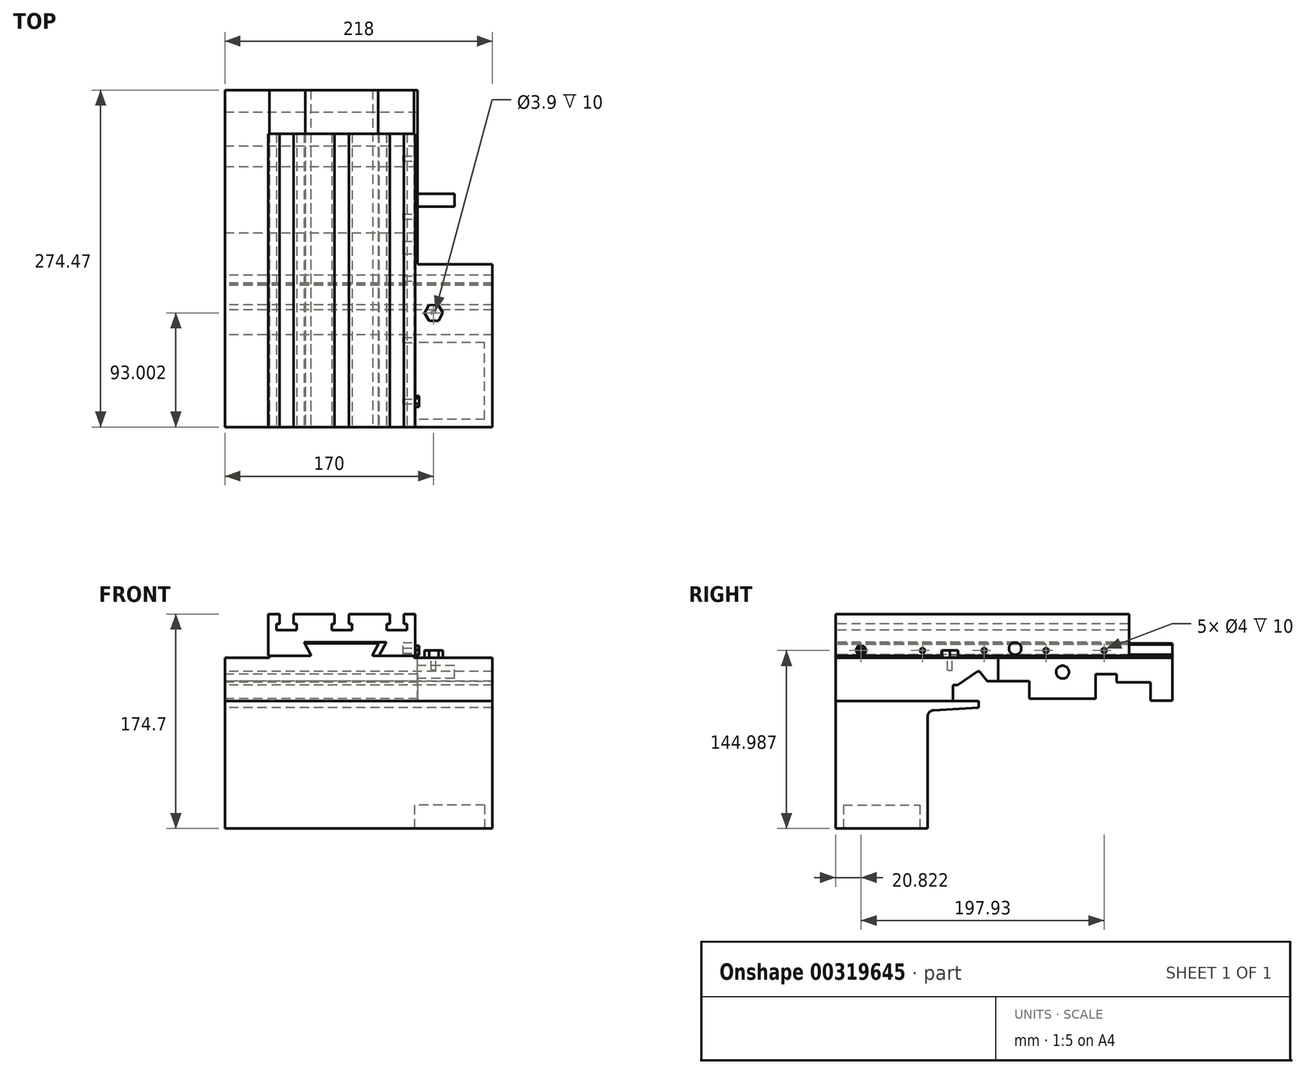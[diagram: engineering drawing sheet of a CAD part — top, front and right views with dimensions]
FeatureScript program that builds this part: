
annotation { "Feature Type Name" : "Feature", "Feature Type Description" : "" }
export const myFeature = defineFeature(function(context is Context, id is Id, definition is map)
    precondition{}
    {
        {
            var Q0;
            Q0=qCreatedBy(makeId("Right.planeOp"),FACE);
            var sketch = newSketch(context, id + "F0", { "sketchPlane" : qUnion([Q0])});
            skLineSegment(sketch, "E0", {"start": v(34.05, 18.4) * mm, "end": v(34.05, 3.4) * mm});
            skLineSegment(sketch, "E1", {"start": v(-63.5, 18.4) * mm, "end": v(-63.5, 3.9) * mm});
            skLineSegment(sketch, "E2", {"start": v(37.05, 18.4) * mm, "end": v(11.3, 18.4) * mm});
            skLineSegment(sketch, "E3", {"start": v(-63.5, 18.4) * mm, "end": v(-90.75, 18.4) * mm});
            skLineSegment(sketch, "E4", {"start": v(-96.5, 16.9) * mm, "end": v(-96.5, 20.4) * mm});
            skLineSegment(sketch, "E5", {"start": v(-96.5, 16.9) * mm, "end": v(-92.5, 16.9) * mm});
            skLineSegment(sketch, "E6", {"start": v(-63.5, 3.9) * mm, "end": v(-72.5, 3.9) * mm});
            skLineSegment(sketch, "E7", {"start": v(-72.5, 3.9) * mm, "end": v(-72.5, -0.6) * mm});
            skLineSegment(sketch, "E8", {"start": v(-90.75, 18.4) * mm, "end": v(-92.5, 16.9) * mm});
            skLineSegment(sketch, "E9", {"start": v(-95.7, 19.4) * mm, "end": v(-102.04, 27.24) * mm});
            skLineSegment(sketch, "E10", {"start": v(-100.9, 25.84) * mm, "end": v(-105.9, 25.84) * mm});
            skLineSegment(sketch, "E11", {"start": v(-103.87, 27.24) * mm, "end": v(-119.92, 16.2) * mm});
            skLineSegment(sketch, "E12", {"start": v(-119.92, 16.2) * mm, "end": v(-119.92, 3.2) * mm});
            skLineSegment(sketch, "E13", {"start": v(-119.92, 3.2) * mm, "end": v(-102.42, 3.2) * mm});
            skLineSegment(sketch, "E14", {"start": v(-102.42, 3.2) * mm, "end": v(-102.42, -78.79) * mm});
            skLineSegment(sketch, "E15", {"start": v(-63.5, 3.9) * mm, "end": v(-5.5, 3.9) * mm, "construction": true});
            skLineSegment(sketch, "E16", {"start": v(34.05, 3.4) * mm, "end": v(27.24, 3.4) * mm});
            skLineSegment(sketch, "E17", {"start": v(27.24, 3.4) * mm, "end": v(27.24, -9.6) * mm});
            skLineSegment(sketch, "E18", {"start": v(27.24, -9.6) * mm, "end": v(34.05, -9.6) * mm});
            skLineSegment(sketch, "E19", {"start": v(34.5, -52.05) * mm, "end": v(32.25, -52.05) * mm});
            skLineSegment(sketch, "E20", {"start": v(32.25, -62.55) * mm, "end": v(34.5, -62.55) * mm});
            skLineSegment(sketch, "E21", {"start": v(5.2, 16.9) * mm, "end": v(5.2, 19.4) * mm});
            skLineSegment(sketch, "E22", {"start": v(5.2, 16.9) * mm, "end": v(9.45, 16.9) * mm});
            skLineSegment(sketch, "E23", {"start": v(9.45, 16.9) * mm, "end": v(11.3, 18.4) * mm});
            skLineSegment(sketch, "E24", {"start": v(5.2, 19.4) * mm, "end": v(2.06, 22.9) * mm});
            skLineSegment(sketch, "E25", {"start": v(2.06, 22.9) * mm, "end": v(-1.79, 22.9) * mm});
            skLineSegment(sketch, "E26", {"start": v(-1.79, 22.9) * mm, "end": v(-5.5, 19.05) * mm});
            skLineSegment(sketch, "E27", {"start": v(-5.5, 19.05) * mm, "end": v(-5.5, 3.85) * mm});
            skLineSegment(sketch, "E28", {"start": v(-5.5, 3.9) * mm, "end": v(4.5, 3.9) * mm});
            skLineSegment(sketch, "E29", {"start": v(4.5, 3.9) * mm, "end": v(4.5, -2.35) * mm});
            skLineSegment(sketch, "E30.0", {"start": v(-219.42, 16.2) * mm, "end": v(-219.42, 3.2) * mm});
            skLineSegment(sketch, "E31.0", {"start": v(-123.92, 16.2) * mm, "end": v(-123.92, 3.2) * mm});
            skLineSegment(sketch, "E32", {"start": v(-219.42, 3.2) * mm, "end": v(-123.92, 3.2) * mm});
            skLineSegment(sketch, "E33", {"start": v(-123.92, 16.2) * mm, "end": v(-119.92, 16.2) * mm});
            skLineSegment(sketch, "E34.0", {"start": v(-61.5, 19.4) * mm, "end": v(-95.7, 19.4) * mm});
            skLineSegment(sketch, "E35", {"start": v(-103.87, 27.24) * mm, "end": v(-102.04, 27.24) * mm});
            skLineSegment(sketch, "E36.0", {"start": v(-61.5, 19.4) * mm, "end": v(-61.5, 4.9) * mm});
            skLineSegment(sketch, "E37.0", {"start": v(-7.5, 19.05) * mm, "end": v(-7.5, 4.9) * mm});
            skLineSegment(sketch, "E38.0", {"start": v(9.45, 24.9) * mm, "end": v(-7.5, 24.9) * mm});
            skLineSegment(sketch, "E39.0", {"start": v(-61.5, 4.9) * mm, "end": v(-7.5, 4.9) * mm});
            skLineSegment(sketch, "E40.trimOffspring", {"start": v(-7.5, 3.9) * mm, "end": v(-7.5, 3.85) * mm});
            skLineSegment(sketch, "E41", {"start": v(-7.5, 19.05) * mm, "end": v(-7.5, 24.9) * mm});
            skPoint(sketch, "E42.orphan", {"position": v(-1.79, 24.9) * mm});
            skLineSegment(sketch, "E43", {"start": v(9.45, 24.9) * mm, "end": v(9.45, 18.4) * mm});
            skLineSegment(sketch, "E44", {"start": v(9.45, 18.4) * mm, "end": v(11.3, 18.4) * mm});
            skLineSegment(sketch, "E45.0", {"start": v(37.05, 18.4) * mm, "end": v(37.05, 3.4) * mm});
            skLineSegment(sketch, "E46.0", {"start": v(55.05, 38.2) * mm, "end": v(55.05, 3.4) * mm});
            skLineSegment(sketch, "E47", {"start": v(37.05, 3.4) * mm, "end": v(55.05, 3.4) * mm});
            skLineSegment(sketch, "E48", {"start": v(55.05, 38.2) * mm, "end": v(-219.42, 38.2) * mm});
            skLineSegment(sketch, "E49", {"start": v(-219.42, 38.2) * mm, "end": v(-219.42, 16.2) * mm});
            skSolve(sketch);
        }
        {
            var Q0;
            Q0=makeQuery(id+"F0.imprint","IMPRINT",FACE,{"disambiguationData":[TD([[makeQuery(id+"F0.imprint","IMPRINT",EDGE,{"derivedFrom":sQuery(id+"F0.wireOp",EDGE,"E30.0")}),1.0]])]});
            extrude(context, id + "F1", {"entities" : qUnion([Q0]), "depth" : 218 * mm});
        }
        {
            var Q0;
            Q0=makeQuery(id+"F1.opExtrude","SWEPT_FACE",FACE,{"disambiguationData":[OSD([sQuery(id+"F0.wireOp",EDGE,"E30.0"),sQuery(id+"F0.wireOp",EDGE,"E49")])]});
            var sketch = newSketch(context, id + "F2", { "sketchPlane" : qUnion([Q0])});
            skPoint(sketch, "E50.0", {"position": v(0, 38.2) * mm});
            skLineSegment(sketch, "E51", {"start": v(0, 38.2) * mm, "end": v(36.15, 38.2) * mm, "construction": true});
            skLineSegment(sketch, "E52", {"start": v(36.15, 38.2) * mm, "end": v(36.15, 39.8) * mm, "construction": true});
            skLineSegment(sketch, "E53", {"start": v(36.15, 39.8) * mm, "end": v(154.15, 39.8) * mm});
            skLineSegment(sketch, "E54", {"start": v(154.15, 39.8) * mm, "end": v(154.15, 38.2) * mm});
            skLineSegment(sketch, "E55", {"start": v(154.15, 38.2) * mm, "end": v(36.15, 38.2) * mm});
            skPoint(sketch, "E56", {"position": v(69.9, 39.8) * mm});
            skPoint(sketch, "E57", {"position": v(120.4, 39.8) * mm});
            skLineSegment(sketch, "E58", {"start": v(95.15, 39.8) * mm, "end": v(95.15, 50.1) * mm, "construction": true});
            skLineSegment(sketch, "E59", {"start": v(65.43, 50.1) * mm, "end": v(95.15, 50.1) * mm});
            skLineSegment(sketch, "E60", {"start": v(95.15, 50.1) * mm, "end": v(124.87, 50.1) * mm});
            skLineSegment(sketch, "E61", {"start": v(36.15, 39.8) * mm, "end": v(36.15, 38.2) * mm});
            skLineSegment(sketch, "E62", {"start": v(69.9, 39.8) * mm, "end": v(69.9, 40.8) * mm});
            skLineSegment(sketch, "E63", {"start": v(65.43, 50.1) * mm, "end": v(65.43, 49.1) * mm});
            skLineSegment(sketch, "E64", {"start": v(124.87, 50.1) * mm, "end": v(124.87, 49.1) * mm});
            skLineSegment(sketch, "E65", {"start": v(120.4, 39.8) * mm, "end": v(120.4, 40.8) * mm});
            skLineSegment(sketch, "E66", {"start": v(65.43, 49.1) * mm, "end": v(69.9, 40.8) * mm});
            skLineSegment(sketch, "E67", {"start": v(124.87, 49.1) * mm, "end": v(120.4, 40.8) * mm});
            skSolve(sketch);
        }
        {
            var Q0;
            {var subQ0=sQuery(id+"F2.wireOp",EDGE,"E54");Q0=makeQuery(id+"F2.imprint","IMPRINT",FACE,{"disambiguationData":[TD([[makeQuery(id+"F2.imprint","IMPRINT",EDGE,{"derivedFrom":subQ0}),-1.0]])]});}
            var Q1;
            Q1=makeQuery(id+"F2.imprint","IMPRINT",FACE,{"disambiguationData":[TD([[makeQuery(id+"F2.imprint","IMPRINT",EDGE,{"derivedFrom":sQuery(id+"F2.wireOp",EDGE,"E59")}),-1.0]])]});
            var Q2;
            Q2=makeQuery(id+"F1.opExtrude","SWEPT_FACE",FACE,{"disambiguationData":[OSD([sQuery(id+"F0.wireOp",EDGE,"E46.0")])]});
            extrude(context, id + "F3", {"entities" : qUnion([Q0, Q1]), "operationType" : NewBodyOperationType.ADD, "endBound" : BoundingType.UP_TO_SURFACE, "oppositeDirection" : true, "endBoundEntityFace" : qUnion([Q2]), "depth" : 25 * mm});
        }
        {
            var Q0;
            {var subQ10=sQuery(id+"F2.wireOp",EDGE,"E54");var subQ15=sQuery(id+"F0.wireOp",EDGE,"E48");Q0=makeQuery(id+"F3.boolean.opBoolean","SPLIT",FACE,{"disambiguationData":[TD([makeQuery(id+"F3.opExtrude","SWEPT_FACE",FACE,{"disambiguationData":[OSD([subQ10])]})])],"derivedFrom":makeQuery(id+"F1.opExtrude","SWEPT_FACE",FACE,{"disambiguationData":[OSD([subQ15])]})});}
            var sketch = newSketch(context, id + "F4", { "sketchPlane" : qUnion([Q0])});
            skPoint(sketch, "E68.0", {"position": v(218, 55.05) * mm});
            skLineSegment(sketch, "E69", {"start": v(218, 55.05) * mm, "end": v(218, -86.95) * mm});
            skLineSegment(sketch, "E70", {"start": v(218, -86.95) * mm, "end": v(157, -86.95) * mm});
            skLineSegment(sketch, "E71", {"start": v(157, -86.95) * mm, "end": v(157, 55.05) * mm});
            skLineSegment(sketch, "E72", {"start": v(157, 55.05) * mm, "end": v(218, 55.05) * mm});
            skSolve(sketch);
        }
        {
            var Q0;
            Q0=makeQuery(id+"F4.imprint","IMPRINT",FACE,{"disambiguationData":[TD([[makeQuery(id+"F4.imprint","IMPRINT",EDGE,{"derivedFrom":sQuery(id+"F4.wireOp",EDGE,"E69")}),-1.0]])]});
            var Q1;
            Q1=makeQuery(id+"F1.opExtrude","SWEPT_FACE",FACE,{"disambiguationData":[OSD([sQuery(id+"F0.wireOp",EDGE,"E47")])]});
            extrude(context, id + "F5", {"entities" : qUnion([Q0]), "operationType" : NewBodyOperationType.REMOVE, "endBound" : BoundingType.UP_TO_SURFACE, "oppositeDirection" : true, "endBoundEntityFace" : qUnion([Q1]), "depth" : 25 * mm});
        }
        {
            var Q0;
            Q0=makeQuery(id+"F3.boolean.opBoolean","MERGE",FACE,{"derivedFrom":[makeQuery(id+"F1.opExtrude","SWEPT_FACE",FACE,{"disambiguationData":[OSD([sQuery(id+"F0.wireOp",EDGE,"E30.0"),sQuery(id+"F0.wireOp",EDGE,"E49")])]}),makeQuery(id+"F3.opExtrude","CAP_FACE",FACE,{"disambiguationData":[OSD([sQuery(id+"F2.wireOp",EDGE,"E53"),sQuery(id+"F2.wireOp",EDGE,"E54"),sQuery(id+"F2.wireOp",EDGE,"E55"),sQuery(id+"F2.wireOp",EDGE,"E59"),sQuery(id+"F2.wireOp",EDGE,"E60"),sQuery(id+"F2.wireOp",EDGE,"E61"),sQuery(id+"F2.wireOp",EDGE,"E62"),sQuery(id+"F2.wireOp",EDGE,"E63"),sQuery(id+"F2.wireOp",EDGE,"E64"),sQuery(id+"F2.wireOp",EDGE,"E65"),sQuery(id+"F2.wireOp",EDGE,"E66"),sQuery(id+"F2.wireOp",EDGE,"E67")])],"isStart":true})]});
            var sketch = newSketch(context, id + "F6", { "sketchPlane" : qUnion([Q0])});
            skLineSegment(sketch, "E73.0", {"start": v(65.43, 50.1) * mm, "end": v(124.87, 50.1) * mm, "construction": true});
            skLineSegment(sketch, "E74", {"start": v(95.15, 50.1) * mm, "end": v(95.15, 39.8) * mm, "construction": true});
            skLineSegment(sketch, "E75", {"start": v(35.25, 39.8) * mm, "end": v(70.44, 39.8) * mm});
            skLineSegment(sketch, "E76", {"start": v(35.25, 39.8) * mm, "end": v(35.25, 73.9) * mm});
            skLineSegment(sketch, "E77", {"start": v(35.25, 73.9) * mm, "end": v(44.55, 73.9) * mm});
            skLineSegment(sketch, "E78", {"start": v(155.05, 73.9) * mm, "end": v(155.05, 39.8) * mm});
            skLineSegment(sketch, "E79.0", {"start": v(64.35, 51.1) * mm, "end": v(131.63, 51.1) * mm});
            skLineSegment(sketch, "E80.0", {"start": v(131.63, 51.1) * mm, "end": v(125.54, 39.8) * mm});
            skLineSegment(sketch, "E81.0", {"start": v(64.35, 51.1) * mm, "end": v(70.44, 39.8) * mm});
            skPoint(sketch, "E82.orphan", {"position": v(65.43, 49.1) * mm});
            skPoint(sketch, "E83.orphan", {"position": v(69.9, 40.8) * mm});
            skLineSegment(sketch, "E84", {"start": v(145.75, 73.9) * mm, "end": v(155.05, 73.9) * mm});
            skLineSegment(sketch, "E85", {"start": v(145.75, 73.9) * mm, "end": v(145.75, 65.9) * mm});
            skLineSegment(sketch, "E86", {"start": v(145.75, 65.9) * mm, "end": v(148.25, 65.9) * mm});
            skLineSegment(sketch, "E87", {"start": v(148.25, 65.9) * mm, "end": v(148.25, 60.9) * mm});
            skLineSegment(sketch, "E88", {"start": v(148.25, 60.9) * mm, "end": v(131.75, 60.9) * mm});
            skLineSegment(sketch, "E89", {"start": v(131.75, 60.9) * mm, "end": v(131.75, 65.9) * mm});
            skLineSegment(sketch, "E90", {"start": v(131.75, 65.9) * mm, "end": v(134.25, 65.9) * mm});
            skLineSegment(sketch, "E91", {"start": v(134.25, 65.9) * mm, "end": v(134.25, 73.9) * mm});
            skLineSegment(sketch, "E92", {"start": v(134.25, 73.9) * mm, "end": v(100.9, 73.9) * mm});
            skLineSegment(sketch, "E93", {"start": v(100.9, 73.9) * mm, "end": v(100.9, 65.9) * mm});
            skLineSegment(sketch, "E94", {"start": v(100.9, 65.9) * mm, "end": v(103.4, 65.9) * mm});
            skLineSegment(sketch, "E95", {"start": v(103.4, 65.9) * mm, "end": v(103.4, 60.9) * mm});
            skLineSegment(sketch, "E96", {"start": v(103.4, 60.9) * mm, "end": v(86.9, 60.9) * mm});
            skLineSegment(sketch, "E97", {"start": v(86.9, 60.9) * mm, "end": v(86.9, 65.9) * mm});
            skLineSegment(sketch, "E98", {"start": v(86.9, 65.9) * mm, "end": v(89.4, 65.9) * mm});
            skLineSegment(sketch, "E99", {"start": v(89.4, 65.9) * mm, "end": v(89.4, 73.9) * mm});
            skLineSegment(sketch, "E100", {"start": v(44.55, 73.9) * mm, "end": v(44.55, 65.9) * mm});
            skLineSegment(sketch, "E101", {"start": v(44.55, 65.9) * mm, "end": v(42.05, 65.9) * mm});
            skLineSegment(sketch, "E102", {"start": v(42.05, 65.9) * mm, "end": v(42.05, 60.9) * mm});
            skLineSegment(sketch, "E103", {"start": v(42.05, 60.9) * mm, "end": v(58.55, 60.9) * mm});
            skLineSegment(sketch, "E104", {"start": v(58.55, 60.9) * mm, "end": v(58.55, 65.9) * mm});
            skLineSegment(sketch, "E105", {"start": v(58.55, 65.9) * mm, "end": v(56.05, 65.9) * mm});
            skLineSegment(sketch, "E106", {"start": v(56.05, 65.9) * mm, "end": v(56.05, 73.9) * mm});
            skLineSegment(sketch, "E107", {"start": v(56.05, 73.9) * mm, "end": v(89.4, 73.9) * mm});
            skLineSegment(sketch, "E108.trimOffspring", {"start": v(125.54, 39.8) * mm, "end": v(155.05, 39.8) * mm});
            skSolve(sketch);
        }
        {
            var Q0;
            {var subQ0=sQuery(id+"F6.wireOp",EDGE,"E76");Q0=makeQuery(id+"F6.imprint","IMPRINT",FACE,{"disambiguationData":[TD([[makeQuery(id+"F6.imprint","IMPRINT",EDGE,{"derivedFrom":subQ0}),-1.0]])]});}
            extrude(context, id + "F7", {"entities" : qUnion([Q0]), "oppositeDirection" : true, "depth" : 239 * mm});
        }
        {
            var Q0;
            Q0=makeQuery(id+"F5.boolean.opBoolean","COPY",FACE,{"derivedFrom":makeQuery(id+"F5.opExtrude","SWEPT_FACE",FACE,{"disambiguationData":[OSD([sQuery(id+"F4.wireOp",EDGE,"E71")])]})});
            var sketch = newSketch(context, id + "F8", { "sketchPlane" : qUnion([Q0])});
            skLineSegment(sketch, "E109.0", {"start": v(-61.5, 4.9) * mm, "end": v(-7.5, 4.9) * mm, "construction": true});
            skLineSegment(sketch, "E110", {"start": v(-34.5, 4.9) * mm, "end": v(-34.5, 38.2) * mm, "construction": true});
            skPoint(sketch, "E111", {"position": v(-34.5, 26.6) * mm});
            skCircle(sketch, "E112", {"center": v(-34.5, 26.6) * mm, "radius": 5.25 * mm});
            skSolve(sketch);
        }
        {
            var Q0;
            Q0=makeQuery(id+"F8.imprint","IMPRINT",FACE,{"disambiguationData":[TD([[makeQuery(id+"F8.imprint","IMPRINT",EDGE,{"derivedFrom":sQuery(id+"F8.wireOp",EDGE,"E112")}),1.0]])]});
            extrude(context, id + "F9", {"entities" : qUnion([Q0]), "operationType" : NewBodyOperationType.ADD, "depth" : 30 * mm});
        }
        {
            var Q0;
            Q0=makeQuery(id+"F7.opExtrude","SWEPT_FACE",FACE,{"disambiguationData":[OSD([sQuery(id+"F6.wireOp",EDGE,"E78")])]});
            var sketch = newSketch(context, id + "F10", { "sketchPlane" : qUnion([Q0])});
            skLineSegment(sketch, "E113.0", {"start": v(19.58, 44.2) * mm, "end": v(-219.42, 44.2) * mm, "construction": true});
            skPoint(sketch, "E114", {"position": v(-198.6, 44.2) * mm});
            skPoint(sketch, "E115", {"position": v(-148.6, 44.2) * mm});
            skPoint(sketch, "E116", {"position": v(-98.35, 44.2) * mm});
            skPoint(sketch, "E117", {"position": v(-47.95, 44.2) * mm});
            skPoint(sketch, "E118", {"position": v(-0.67, 44.2) * mm});
            skCircle(sketch, "E119", {"center": v(-198.6, 44.2) * mm, "radius": 2 * mm});
            skCircle(sketch, "E120", {"center": v(-148.6, 44.2) * mm, "radius": 2 * mm});
            skCircle(sketch, "E121", {"center": v(-98.35, 44.2) * mm, "radius": 2 * mm});
            skCircle(sketch, "E122", {"center": v(-47.95, 44.2) * mm, "radius": 2 * mm});
            skCircle(sketch, "E123", {"center": v(-0.67, 44.2) * mm, "radius": 2 * mm});
            skPoint(sketch, "E124", {"position": v(-73.15, 45.8) * mm});
            skCircle(sketch, "E125", {"center": v(-73.15, 45.8) * mm, "radius": 5 * mm});
            skCircle(sketch, "E126.cCircle", {"center": v(-198.6, 44.2) * mm, "radius": 3.83 * mm, "construction": true});
            skLineSegment(sketch, "E126.0", {"start": v(-196.11, 47.86) * mm, "end": v(-194.19, 43.88) * mm});
            skLineSegment(sketch, "E126.1", {"start": v(-194.19, 43.88) * mm, "end": v(-196.67, 40.22) * mm});
            skLineSegment(sketch, "E126.2", {"start": v(-196.67, 40.22) * mm, "end": v(-201.08, 40.54) * mm});
            skLineSegment(sketch, "E126.3", {"start": v(-201.08, 40.54) * mm, "end": v(-203, 44.52) * mm});
            skLineSegment(sketch, "E126.4", {"start": v(-203, 44.52) * mm, "end": v(-200.53, 48.18) * mm});
            skLineSegment(sketch, "E126.5", {"start": v(-200.53, 48.18) * mm, "end": v(-196.11, 47.86) * mm});
            skPoint(sketch, "E126.0.midPoint", {"position": v(-195.15, 45.87) * mm});
            skSolve(sketch);
        }
        {
            var Q0;
            Q0=makeQuery(id+"F10.imprint","IMPRINT",FACE,{"disambiguationData":[TD([[makeQuery(id+"F10.imprint","IMPRINT",EDGE,{"derivedFrom":sQuery(id+"F10.wireOp",EDGE,"E119")}),1.0]])]});
            var Q1;
            Q1=makeQuery(id+"F10.imprint","IMPRINT",FACE,{"disambiguationData":[TD([[makeQuery(id+"F10.imprint","IMPRINT",EDGE,{"derivedFrom":sQuery(id+"F10.wireOp",EDGE,"E120")}),1.0]])]});
            var Q2;
            Q2=makeQuery(id+"F10.imprint","IMPRINT",FACE,{"disambiguationData":[TD([[makeQuery(id+"F10.imprint","IMPRINT",EDGE,{"derivedFrom":sQuery(id+"F10.wireOp",EDGE,"E121")}),1.0]])]});
            var Q3;
            Q3=makeQuery(id+"F10.imprint","IMPRINT",FACE,{"disambiguationData":[TD([[makeQuery(id+"F10.imprint","IMPRINT",EDGE,{"derivedFrom":sQuery(id+"F10.wireOp",EDGE,"E122")}),1.0]])]});
            var Q4;
            Q4=makeQuery(id+"F10.imprint","IMPRINT",FACE,{"disambiguationData":[TD([[makeQuery(id+"F10.imprint","IMPRINT",EDGE,{"derivedFrom":sQuery(id+"F10.wireOp",EDGE,"E123")}),1.0]])]});
            var Q5;
            Q5=makeQuery(id+"F10.imprint","IMPRINT",FACE,{"disambiguationData":[TD([[makeQuery(id+"F10.imprint","IMPRINT",EDGE,{"derivedFrom":sQuery(id+"F10.wireOp",EDGE,"E125")}),1.0]])]});
            extrude(context, id + "F11", {"entities" : qUnion([Q0, Q1, Q2, Q3, Q4, Q5]), "operationType" : NewBodyOperationType.REMOVE, "oppositeDirection" : true, "depth" : 10 * mm});
        }
        {
            var Q0;
            Q0=makeQuery(id+"F10.imprint","IMPRINT",FACE,{"disambiguationData":[TD([[makeQuery(id+"F10.imprint","IMPRINT",EDGE,{"derivedFrom":sQuery(id+"F10.wireOp",EDGE,"E119")}),-1.0]])]});
            extrude(context, id + "F12", {"entities" : qUnion([Q0]), "depth" : 3.25 * mm});
        }
        {
            var Q0;
            {var subQ10=sQuery(id+"F2.wireOp",EDGE,"E54");var subQ15=sQuery(id+"F0.wireOp",EDGE,"E48");Q0=makeQuery(id+"F3.boolean.opBoolean","SPLIT",FACE,{"disambiguationData":[TD([makeQuery(id+"F3.opExtrude","SWEPT_FACE",FACE,{"disambiguationData":[OSD([subQ10])]})])],"derivedFrom":makeQuery(id+"F1.opExtrude","SWEPT_FACE",FACE,{"disambiguationData":[OSD([subQ15])]})});}
            var sketch = newSketch(context, id + "F13", { "sketchPlane" : qUnion([Q0])});
            skPoint(sketch, "E127", {"position": v(170, -126.42) * mm});
            skCircle(sketch, "E128.cCircle", {"center": v(170, -126.42) * mm, "radius": 6.5 * mm, "construction": true});
            skLineSegment(sketch, "E128.0", {"start": v(173.57, -119.82) * mm, "end": v(177.5, -126.21) * mm});
            skLineSegment(sketch, "E128.1", {"start": v(177.5, -126.21) * mm, "end": v(173.93, -132.81) * mm});
            skLineSegment(sketch, "E128.2", {"start": v(173.93, -132.81) * mm, "end": v(166.43, -133.02) * mm});
            skLineSegment(sketch, "E128.3", {"start": v(166.43, -133.02) * mm, "end": v(162.5, -126.62) * mm});
            skLineSegment(sketch, "E128.4", {"start": v(162.5, -126.62) * mm, "end": v(166.07, -120.02) * mm});
            skLineSegment(sketch, "E128.5", {"start": v(166.07, -120.02) * mm, "end": v(173.57, -119.82) * mm});
            skPoint(sketch, "E128.0.midPoint", {"position": v(175.54, -123.01) * mm});
            skCircle(sketch, "E129", {"center": v(170, -126.42) * mm, "radius": 1.95 * mm});
            skSolve(sketch);
        }
        {
            var Q0;
            Q0=makeQuery(id+"F13.imprint","IMPRINT",FACE,{"disambiguationData":[TD([[makeQuery(id+"F13.imprint","IMPRINT",EDGE,{"derivedFrom":sQuery(id+"F13.wireOp",EDGE,"E128.0")}),-1.0]])]});
            var Q1;
            Q1=makeQuery(id+"F13.imprint","IMPRINT",FACE,{"disambiguationData":[TD([[makeQuery(id+"F13.imprint","IMPRINT",EDGE,{"derivedFrom":sQuery(id+"F13.wireOp",EDGE,"E129")}),1.0]])]});
            extrude(context, id + "F14", {"entities" : qUnion([Q0, Q1]), "depth" : 6 * mm});
        }
        {
            var Q0;
            Q0=makeQuery(id+"F13.imprint","IMPRINT",FACE,{"disambiguationData":[TD([[makeQuery(id+"F13.imprint","IMPRINT",EDGE,{"derivedFrom":sQuery(id+"F13.wireOp",EDGE,"E129")}),1.0]])]});
            extrude(context, id + "F15", {"entities" : qUnion([Q0]), "operationType" : NewBodyOperationType.REMOVE, "oppositeDirection" : true, "depth" : 10 * mm});
        }
        {
            var Q0;
            Q0=makeQuery(id+"F1.opExtrude","CAP_FACE",FACE,{"disambiguationData":[OSD([sQuery(id+"F0.wireOp",EDGE,"E2"),sQuery(id+"F0.wireOp",EDGE,"E9"),sQuery(id+"F0.wireOp",EDGE,"E11"),sQuery(id+"F0.wireOp",EDGE,"E30.0"),sQuery(id+"F0.wireOp",EDGE,"E31.0"),sQuery(id+"F0.wireOp",EDGE,"E32"),sQuery(id+"F0.wireOp",EDGE,"E33"),sQuery(id+"F0.wireOp",EDGE,"E34.0"),sQuery(id+"F0.wireOp",EDGE,"E35"),sQuery(id+"F0.wireOp",EDGE,"E36.0"),sQuery(id+"F0.wireOp",EDGE,"E37.0"),sQuery(id+"F0.wireOp",EDGE,"E38.0"),sQuery(id+"F0.wireOp",EDGE,"E39.0"),sQuery(id+"F0.wireOp",EDGE,"E41"),sQuery(id+"F0.wireOp",EDGE,"E43"),sQuery(id+"F0.wireOp",EDGE,"E44"),sQuery(id+"F0.wireOp",EDGE,"E45.0"),sQuery(id+"F0.wireOp",EDGE,"E46.0"),sQuery(id+"F0.wireOp",EDGE,"E47"),sQuery(id+"F0.wireOp",EDGE,"E48"),sQuery(id+"F0.wireOp",EDGE,"E49")])],"isStart":true});
            var sketch = newSketch(context, id + "F16", { "sketchPlane" : qUnion([Q0])});
            skPoint(sketch, "E130.0", {"position": v(219.42, 3.2) * mm});
            skLineSegment(sketch, "E131", {"start": v(219.42, 3.2) * mm, "end": v(102.92, 3.2) * mm});
            skPoint(sketch, "E131.endSnap0", {"position": v(171.67, 3.2) * mm});
            skLineSegment(sketch, "E132", {"start": v(102.92, 3.2) * mm, "end": v(102.92, -2.3) * mm});
            skLineSegment(sketch, "E133", {"start": v(219.42, 3.2) * mm, "end": v(219.42, -100.8) * mm});
            skLineSegment(sketch, "E134", {"start": v(219.42, -100.8) * mm, "end": v(144.42, -100.8) * mm});
            skLineSegment(sketch, "E135", {"start": v(144.42, -100.8) * mm, "end": v(144.42, -9.5) * mm});
            skLineSegment(sketch, "E136", {"start": v(139.72, -4.5) * mm, "end": v(102.92, -2.3) * mm});
            skPoint(sketch, "E137.visualSharp", {"position": v(144.42, -4.8) * mm});
            skArc(sketch, "E137.filletArc", {"start": v(144.42, -9.5) * mm, "mid": v(143.06, -6.07) * mm, "end": v(139.72, -4.5) * mm});
            skSolve(sketch);
        }
        {
            var Q0;
            {var subQ1=sQuery(id+"F16.wireOp",EDGE,"E132");Q0=makeQuery(id+"F16.imprint","IMPRINT",FACE,{"disambiguationData":[TD([[makeQuery(id+"F16.imprint","IMPRINT",EDGE,{"derivedFrom":subQ1}),1.0]])]});}
            var Q1;
            Q1=makeQuery(id+"F1.opExtrude","CAP_FACE",FACE,{"disambiguationData":[OSD([sQuery(id+"F0.wireOp",EDGE,"E2"),sQuery(id+"F0.wireOp",EDGE,"E9"),sQuery(id+"F0.wireOp",EDGE,"E11"),sQuery(id+"F0.wireOp",EDGE,"E30.0"),sQuery(id+"F0.wireOp",EDGE,"E31.0"),sQuery(id+"F0.wireOp",EDGE,"E32"),sQuery(id+"F0.wireOp",EDGE,"E33"),sQuery(id+"F0.wireOp",EDGE,"E34.0"),sQuery(id+"F0.wireOp",EDGE,"E35"),sQuery(id+"F0.wireOp",EDGE,"E36.0"),sQuery(id+"F0.wireOp",EDGE,"E37.0"),sQuery(id+"F0.wireOp",EDGE,"E38.0"),sQuery(id+"F0.wireOp",EDGE,"E39.0"),sQuery(id+"F0.wireOp",EDGE,"E41"),sQuery(id+"F0.wireOp",EDGE,"E43"),sQuery(id+"F0.wireOp",EDGE,"E44"),sQuery(id+"F0.wireOp",EDGE,"E45.0"),sQuery(id+"F0.wireOp",EDGE,"E46.0"),sQuery(id+"F0.wireOp",EDGE,"E47"),sQuery(id+"F0.wireOp",EDGE,"E48"),sQuery(id+"F0.wireOp",EDGE,"E49")])],"isStart":false});
            extrude(context, id + "F17", {"entities" : qUnion([Q0]), "endBound" : BoundingType.UP_TO_SURFACE, "oppositeDirection" : true, "endBoundEntityFace" : qUnion([Q1]), "depth" : 25 * mm});
        }
        {
            var Q0;
            Q0=makeQuery(id+"F17.opExtrude","SWEPT_FACE",FACE,{"disambiguationData":[OSD([sQuery(id+"F16.wireOp",EDGE,"E134")])]});
            var sketch = newSketch(context, id + "F18", { "sketchPlane" : qUnion([Q0])});
            skLineSegment(sketch, "E138.0", {"start": v(218, 219.42) * mm, "end": v(154.5, 219.42) * mm});
            skLineSegment(sketch, "E139.0", {"start": v(218, 219.42) * mm, "end": v(218, 144.42) * mm});
            skLineSegment(sketch, "E140.0", {"start": v(218, 144.42) * mm, "end": v(154.5, 144.42) * mm});
            skLineSegment(sketch, "E141.0", {"start": v(154.5, 219.42) * mm, "end": v(154.5, 144.42) * mm});
            skPoint(sketch, "E142.orphan", {"position": v(0, 219.42) * mm});
            skPoint(sketch, "E143.orphan", {"position": v(0, 144.42) * mm});
            skLineSegment(sketch, "E144.0", {"start": v(211.65, 213.07) * mm, "end": v(154.5, 213.07) * mm});
            skLineSegment(sketch, "E144.1", {"start": v(211.65, 213.07) * mm, "end": v(211.65, 150.77) * mm});
            skLineSegment(sketch, "E144.2", {"start": v(211.65, 150.77) * mm, "end": v(154.5, 150.77) * mm});
            skSolve(sketch);
        }
        {
            var Q0;
            {var subQ0=sQuery(id+"F18.wireOp",EDGE,"E144.0");Q0=makeQuery(id+"F18.imprint","IMPRINT",FACE,{"disambiguationData":[TD([[makeQuery(id+"F18.imprint","IMPRINT",EDGE,{"derivedFrom":subQ0}),1.0]])]});}
            extrude(context, id + "F19", {"entities" : qUnion([Q0]), "operationType" : NewBodyOperationType.REMOVE, "oppositeDirection" : true, "depth" : 19.05 * mm});
        }
    });
